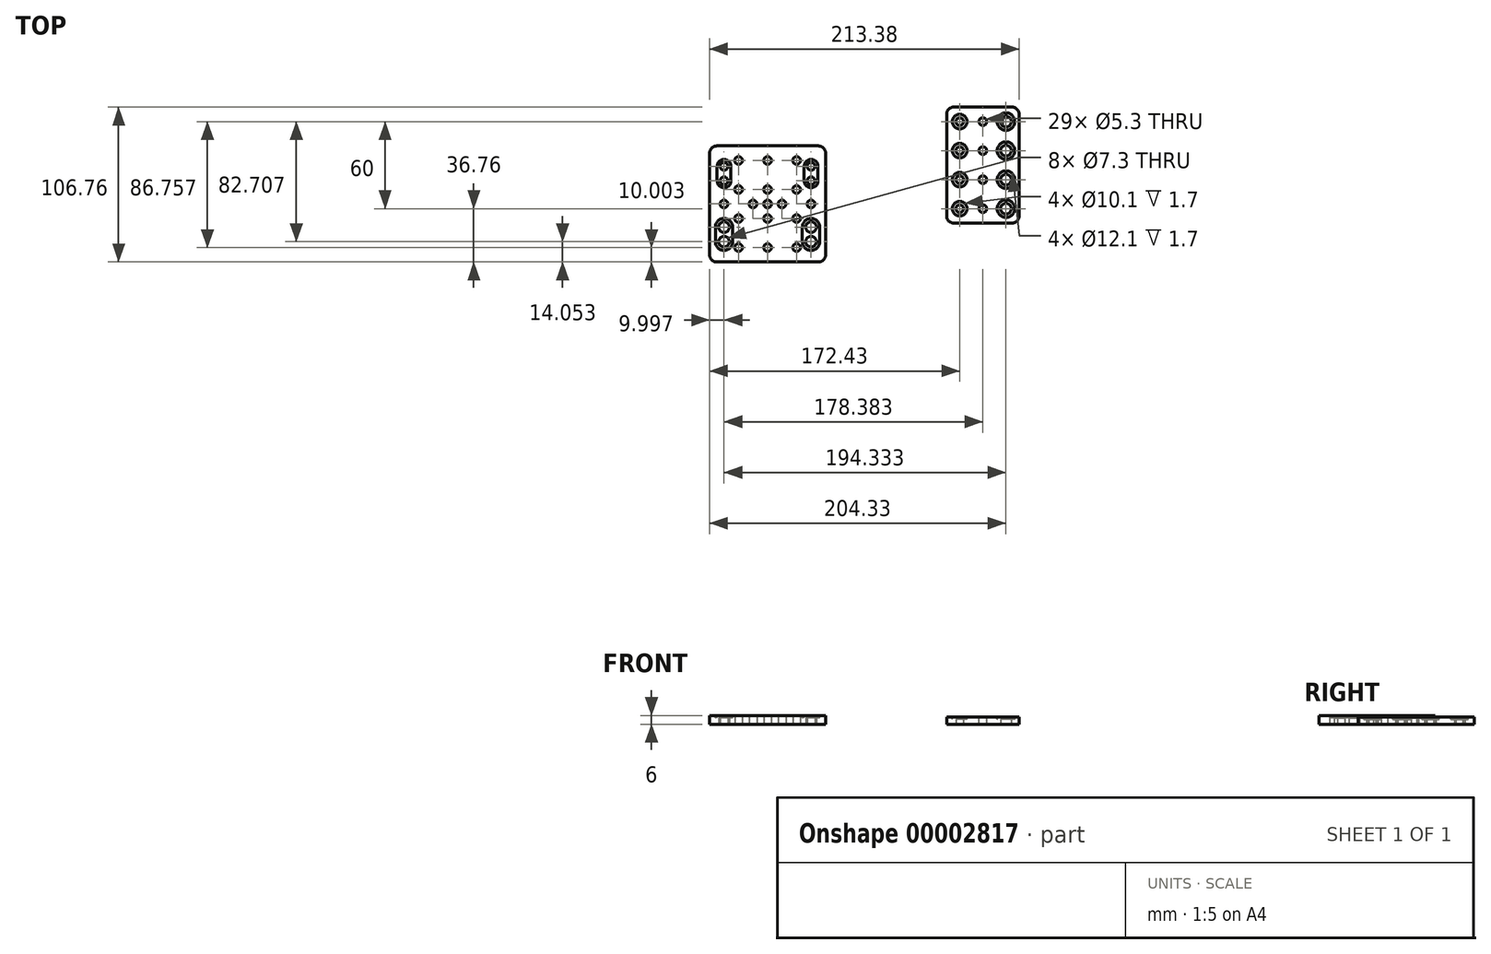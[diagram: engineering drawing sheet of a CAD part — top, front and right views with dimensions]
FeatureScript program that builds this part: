
annotation { "Feature Type Name" : "Feature", "Feature Type Description" : "" }
export const myFeature = defineFeature(function(context is Context, id is Id, definition is map)
    precondition{}
    {
        {
            var Q0;
            Q0=qCreatedBy(makeId("Top.planeOp"),FACE);
            var sketch = newSketch(context, id + "F0", { "sketchPlane" : qUnion([Q0])});
            skLineSegment(sketch, "E0.rect.bottom", {"start": v(-15.95, 60) * mm, "end": v(15.95, 60) * mm, "construction": true});
            skLineSegment(sketch, "E0.rect.top", {"start": v(-15.95, -60) * mm, "end": v(15.95, -60) * mm, "construction": true});
            skLineSegment(sketch, "E0.rect.left", {"start": v(-15.95, 60) * mm, "end": v(-15.95, -60) * mm, "construction": true});
            skLineSegment(sketch, "E0.rect.right", {"start": v(15.95, 60) * mm, "end": v(15.95, -60) * mm, "construction": true});
            skPoint(sketch, "E0.rect.middle", {"position": v(0, 0) * mm});
            skLineSegment(sketch, "E1.rect.bottom", {"start": v(-20, 40) * mm, "end": v(20, 40) * mm});
            skLineSegment(sketch, "E1.rect.top", {"start": v(-20, -40) * mm, "end": v(20, -40) * mm});
            skLineSegment(sketch, "E1.rect.left", {"start": v(-25, 35) * mm, "end": v(-25, -35) * mm});
            skLineSegment(sketch, "E1.rect.right", {"start": v(25, 35) * mm, "end": v(25, -35) * mm});
            skPoint(sketch, "E2.visualSharp", {"position": v(-25, 40) * mm});
            skArc(sketch, "E2.filletArc", {"start": v(-20, 40) * mm, "mid": v(-23.54, 38.54) * mm, "end": v(-25, 35) * mm});
            skPoint(sketch, "E3.visualSharp", {"position": v(25, 40) * mm});
            skArc(sketch, "E3.filletArc", {"start": v(25, 35) * mm, "mid": v(23.54, 38.54) * mm, "end": v(20, 40) * mm});
            skPoint(sketch, "E4.visualSharp", {"position": v(25, -40) * mm});
            skArc(sketch, "E4.filletArc", {"start": v(20, -40) * mm, "mid": v(23.54, -38.54) * mm, "end": v(25, -35) * mm});
            skPoint(sketch, "E5.visualSharp", {"position": v(-25, -40) * mm});
            skArc(sketch, "E5.filletArc", {"start": v(-25, -35) * mm, "mid": v(-23.54, -38.54) * mm, "end": v(-20, -40) * mm});
            skLineSegment(sketch, "E6", {"start": v(0, 40) * mm, "end": v(0, -40) * mm, "construction": true});
            skLineSegment(sketch, "E7", {"start": v(25, 0) * mm, "end": v(-25, 0) * mm, "construction": true});
            skPoint(sketch, "E8", {"position": v(-15.95, 10) * mm});
            skPoint(sketch, "E9", {"position": v(-15.95, 30) * mm});
            skPoint(sketch, "E10", {"position": v(-15.95, -10) * mm});
            skPoint(sketch, "E11", {"position": v(-15.95, -30) * mm});
            skPoint(sketch, "E12.MirrorP", {"position": v(15.95, 30) * mm});
            skPoint(sketch, "E13.MirrorP", {"position": v(15.95, 10) * mm});
            skPoint(sketch, "E14.MirrorP", {"position": v(15.95, -10) * mm});
            skPoint(sketch, "E15.MirrorP", {"position": v(15.95, -30) * mm});
            skCircle(sketch, "E16", {"center": v(-15.95, 30) * mm, "radius": 2.65 * mm});
            skCircle(sketch, "E17", {"center": v(-15.95, 10) * mm, "radius": 2.65 * mm});
            skCircle(sketch, "E18", {"center": v(-15.95, -10) * mm, "radius": 2.65 * mm});
            skCircle(sketch, "E19", {"center": v(-15.95, -30) * mm, "radius": 2.65 * mm});
            skCircle(sketch, "E20", {"center": v(15.95, 30) * mm, "radius": 3.65 * mm});
            skCircle(sketch, "E21", {"center": v(15.95, 10) * mm, "radius": 3.65 * mm});
            skCircle(sketch, "E22", {"center": v(15.95, -10) * mm, "radius": 3.65 * mm});
            skCircle(sketch, "E23", {"center": v(15.95, -30) * mm, "radius": 3.65 * mm});
            skSolve(sketch);
        }
        {
            var Q0;
            Q0 = qSketchRegion(id + "F0", true);
            extrude(context, id + "F1", {"entities" : qUnion([Q0]), "depth" : 5 * mm});
        }
        {
            var Q0;
            Q0=makeQuery(id+"F1.opExtrude","CAP_FACE",FACE,{"disambiguationData":[OSD([sQuery(id+"F0.wireOp",EDGE,"E1.rect.bottom"),sQuery(id+"F0.wireOp",EDGE,"E1.rect.top"),sQuery(id+"F0.wireOp",EDGE,"E1.rect.left"),sQuery(id+"F0.wireOp",EDGE,"E1.rect.right"),sQuery(id+"F0.wireOp",EDGE,"E2.filletArc"),sQuery(id+"F0.wireOp",EDGE,"E3.filletArc"),sQuery(id+"F0.wireOp",EDGE,"E4.filletArc"),sQuery(id+"F0.wireOp",EDGE,"E5.filletArc"),sQuery(id+"F0.wireOp",EDGE,"E16"),sQuery(id+"F0.wireOp",EDGE,"E17"),sQuery(id+"F0.wireOp",EDGE,"E18"),sQuery(id+"F0.wireOp",EDGE,"E19"),sQuery(id+"F0.wireOp",EDGE,"E20"),sQuery(id+"F0.wireOp",EDGE,"E21"),sQuery(id+"F0.wireOp",EDGE,"E22"),sQuery(id+"F0.wireOp",EDGE,"E23")])],"isStart":false});
            var sketch = newSketch(context, id + "F2", { "sketchPlane" : qUnion([Q0])});
            skCircle(sketch, "E24", {"center": v(-15.95, 30) * mm, "radius": 5.05 * mm});
            skCircle(sketch, "E25", {"center": v(-15.95, 10) * mm, "radius": 5.05 * mm});
            skCircle(sketch, "E26", {"center": v(-15.95, -10) * mm, "radius": 5.05 * mm});
            skCircle(sketch, "E27", {"center": v(-15.95, -30) * mm, "radius": 5.05 * mm});
            skCircle(sketch, "E28", {"center": v(15.95, 30) * mm, "radius": 6.05 * mm});
            skCircle(sketch, "E29", {"center": v(15.95, 10) * mm, "radius": 6.05 * mm});
            skCircle(sketch, "E30", {"center": v(15.95, -10) * mm, "radius": 6.05 * mm});
            skCircle(sketch, "E31", {"center": v(15.95, -30) * mm, "radius": 6.05 * mm});
            skSolve(sketch);
        }
        {
            var Q0;
            Q0 = qSketchRegion(id + "F2", true);
            extrude(context, id + "F3", {"entities" : qUnion([Q0]), "operationType" : NewBodyOperationType.REMOVE, "oppositeDirection" : true, "depth" : 1.7 * mm});
        }
        {
            var Q0;
            Q0=makeQuery(id+"F1.opExtrude","CAP_FACE",FACE,{"disambiguationData":[OSD([sQuery(id+"F0.wireOp",EDGE,"E1.rect.bottom"),sQuery(id+"F0.wireOp",EDGE,"E1.rect.top"),sQuery(id+"F0.wireOp",EDGE,"E1.rect.left"),sQuery(id+"F0.wireOp",EDGE,"E1.rect.right"),sQuery(id+"F0.wireOp",EDGE,"E2.filletArc"),sQuery(id+"F0.wireOp",EDGE,"E3.filletArc"),sQuery(id+"F0.wireOp",EDGE,"E4.filletArc"),sQuery(id+"F0.wireOp",EDGE,"E5.filletArc"),sQuery(id+"F0.wireOp",EDGE,"E16"),sQuery(id+"F0.wireOp",EDGE,"E17"),sQuery(id+"F0.wireOp",EDGE,"E18"),sQuery(id+"F0.wireOp",EDGE,"E19"),sQuery(id+"F0.wireOp",EDGE,"E20"),sQuery(id+"F0.wireOp",EDGE,"E21"),sQuery(id+"F0.wireOp",EDGE,"E22"),sQuery(id+"F0.wireOp",EDGE,"E23")])],"isStart":false});
            var sketch = newSketch(context, id + "F4", { "sketchPlane" : qUnion([Q0])});
            skLineSegment(sketch, "E32", {"start": v(0, 40) * mm, "end": v(0, -40) * mm, "construction": true});
            skPoint(sketch, "E33", {"position": v(0, 30) * mm});
            skPoint(sketch, "E34", {"position": v(0, 10) * mm});
            skPoint(sketch, "E35", {"position": v(0, -10) * mm});
            skPoint(sketch, "E36", {"position": v(0, -30) * mm});
            skCircle(sketch, "E37.0", {"center": v(-15.95, 30) * mm, "radius": 2.65 * mm, "construction": true});
            skCircle(sketch, "E38.0", {"center": v(-15.95, 10) * mm, "radius": 2.65 * mm, "construction": true});
            skCircle(sketch, "E39.0", {"center": v(-15.95, -10) * mm, "radius": 2.65 * mm, "construction": true});
            skCircle(sketch, "E40.0", {"center": v(-15.95, -30) * mm, "radius": 2.65 * mm, "construction": true});
            skCircle(sketch, "E41", {"center": v(0, 30) * mm, "radius": 2.65 * mm});
            skCircle(sketch, "E42", {"center": v(0, 10) * mm, "radius": 2.65 * mm});
            skCircle(sketch, "E43", {"center": v(0, -10) * mm, "radius": 2.65 * mm});
            skCircle(sketch, "E44", {"center": v(0, -30) * mm, "radius": 2.65 * mm});
            skSolve(sketch);
        }
        {
            var Q0;
            Q0 = qSketchRegion(id + "F4", true);
            var Q1;
            Q1=makeQuery(id+"F1.opExtrude","CAP_FACE",FACE,{"disambiguationData":[OSD([sQuery(id+"F0.wireOp",EDGE,"E1.rect.bottom"),sQuery(id+"F0.wireOp",EDGE,"E1.rect.top"),sQuery(id+"F0.wireOp",EDGE,"E1.rect.left"),sQuery(id+"F0.wireOp",EDGE,"E1.rect.right"),sQuery(id+"F0.wireOp",EDGE,"E2.filletArc"),sQuery(id+"F0.wireOp",EDGE,"E3.filletArc"),sQuery(id+"F0.wireOp",EDGE,"E4.filletArc"),sQuery(id+"F0.wireOp",EDGE,"E5.filletArc"),sQuery(id+"F0.wireOp",EDGE,"E16"),sQuery(id+"F0.wireOp",EDGE,"E17"),sQuery(id+"F0.wireOp",EDGE,"E18"),sQuery(id+"F0.wireOp",EDGE,"E19"),sQuery(id+"F0.wireOp",EDGE,"E20"),sQuery(id+"F0.wireOp",EDGE,"E21"),sQuery(id+"F0.wireOp",EDGE,"E22"),sQuery(id+"F0.wireOp",EDGE,"E23")])],"isStart":true});
            extrude(context, id + "F5", {"entities" : qUnion([Q0]), "operationType" : NewBodyOperationType.REMOVE, "endBound" : BoundingType.UP_TO_SURFACE, "oppositeDirection" : true, "endBoundEntityFace" : qUnion([Q1]), "depth" : 25 * mm});
        }
        {
            var Q0;
            Q0=qCreatedBy(makeId("Top.planeOp"),FACE);
            var sketch = newSketch(context, id + "F6", { "sketchPlane" : qUnion([Q0])});
            skLineSegment(sketch, "E45", {"start": v(-148.38, 31.47) * mm, "end": v(-148.38, -84.99) * mm, "construction": true});
            skLineSegment(sketch, "E46", {"start": v(-200.91, -26.76) * mm, "end": v(-92.3, -26.76) * mm, "construction": true});
            skPoint(sketch, "E46.startSnap0", {"position": v(-148.38, -26.76) * mm});
            skPoint(sketch, "E47", {"position": v(-178.38, -10.8) * mm});
            skPoint(sketch, "E48", {"position": v(-178.38, -42.7) * mm});
            skPoint(sketch, "E49", {"position": v(-178.38, -52.7) * mm});
            skPoint(sketch, "E50", {"position": v(-178.38, -0.8) * mm});
            skPoint(sketch, "E51", {"position": v(-118.38, -10.8) * mm});
            skPoint(sketch, "E52", {"position": v(-118.38, -0.8) * mm});
            skPoint(sketch, "E53", {"position": v(-118.38, -42.7) * mm});
            skPoint(sketch, "E54", {"position": v(-118.38, -52.7) * mm});
            skCircle(sketch, "E55", {"center": v(-178.38, -0.8) * mm, "radius": 2.65 * mm});
            skCircle(sketch, "E56", {"center": v(-178.38, -10.8) * mm, "radius": 2.65 * mm});
            skCircle(sketch, "E57", {"center": v(-178.38, -42.7) * mm, "radius": 3.65 * mm});
            skCircle(sketch, "E58", {"center": v(-178.38, -52.7) * mm, "radius": 3.65 * mm});
            skCircle(sketch, "E59", {"center": v(-118.38, -0.8) * mm, "radius": 2.65 * mm});
            skCircle(sketch, "E60", {"center": v(-118.38, -10.8) * mm, "radius": 2.65 * mm});
            skCircle(sketch, "E61", {"center": v(-118.38, -42.7) * mm, "radius": 3.65 * mm});
            skCircle(sketch, "E62", {"center": v(-118.38, -52.7) * mm, "radius": 3.65 * mm});
            skPoint(sketch, "E63", {"position": v(-158.38, -26.76) * mm});
            skPoint(sketch, "E64", {"position": v(-178.38, -26.76) * mm});
            skPoint(sketch, "E65", {"position": v(-138.38, -26.76) * mm});
            skPoint(sketch, "E66", {"position": v(-118.38, -26.76) * mm});
            skCircle(sketch, "E67", {"center": v(-178.38, -26.76) * mm, "radius": 2.65 * mm});
            skCircle(sketch, "E68", {"center": v(-158.38, -26.76) * mm, "radius": 2.65 * mm});
            skCircle(sketch, "E69", {"center": v(-148.38, -26.76) * mm, "radius": 2.65 * mm});
            skCircle(sketch, "E70", {"center": v(-138.38, -26.76) * mm, "radius": 2.65 * mm});
            skCircle(sketch, "E71", {"center": v(-118.38, -26.76) * mm, "radius": 2.65 * mm});
            skPoint(sketch, "E72", {"position": v(-148.38, -16.76) * mm});
            skPoint(sketch, "E73", {"position": v(-148.38, -36.76) * mm});
            skPoint(sketch, "E74", {"position": v(-168.38, -36.76) * mm});
            skPoint(sketch, "E75", {"position": v(-168.38, -16.76) * mm});
            skPoint(sketch, "E76", {"position": v(-128.38, -16.76) * mm});
            skPoint(sketch, "E77", {"position": v(-128.38, -36.76) * mm});
            skCircle(sketch, "E78", {"center": v(-168.38, -16.76) * mm, "radius": 2.65 * mm});
            skCircle(sketch, "E79", {"center": v(-148.38, -16.76) * mm, "radius": 2.65 * mm});
            skCircle(sketch, "E80", {"center": v(-128.38, -16.76) * mm, "radius": 2.65 * mm});
            skCircle(sketch, "E81", {"center": v(-128.38, -36.76) * mm, "radius": 2.65 * mm});
            skCircle(sketch, "E82", {"center": v(-148.38, -36.76) * mm, "radius": 2.65 * mm});
            skCircle(sketch, "E83", {"center": v(-168.38, -36.76) * mm, "radius": 2.65 * mm});
            skCircle(sketch, "E84.0.1.0", {"center": v(-168.38, 3.24) * mm, "radius": 2.65 * mm});
            skCircle(sketch, "E84.0.1.1", {"center": v(-148.38, 3.24) * mm, "radius": 2.65 * mm});
            skCircle(sketch, "E84.0.1.2", {"center": v(-128.38, 3.24) * mm, "radius": 2.65 * mm});
            skLineSegment(sketch, "E84.direction1", {"start": v(-168.38, -16.76) * mm, "end": v(-143.38, -16.76) * mm, "construction": true});
            skLineSegment(sketch, "E84.direction2", {"start": v(-168.38, -16.76) * mm, "end": v(-168.38, 3.24) * mm, "construction": true});
            skCircle(sketch, "E85.0.1.0", {"center": v(-168.38, -56.76) * mm, "radius": 2.65 * mm});
            skCircle(sketch, "E85.0.1.1", {"center": v(-148.38, -56.76) * mm, "radius": 2.65 * mm});
            skCircle(sketch, "E85.0.1.2", {"center": v(-128.38, -56.76) * mm, "radius": 2.65 * mm});
            skLineSegment(sketch, "E85.direction1", {"start": v(-168.38, -36.76) * mm, "end": v(-143.38, -36.76) * mm, "construction": true});
            skLineSegment(sketch, "E85.direction2", {"start": v(-168.38, -36.76) * mm, "end": v(-168.38, -56.76) * mm, "construction": true});
            skLineSegment(sketch, "E86.rect.bottom", {"start": v(-188.38, 13.24) * mm, "end": v(-108.38, 13.24) * mm});
            skLineSegment(sketch, "E86.rect.top", {"start": v(-188.38, -66.76) * mm, "end": v(-108.38, -66.76) * mm});
            skLineSegment(sketch, "E86.rect.left", {"start": v(-188.38, 13.24) * mm, "end": v(-188.38, -66.76) * mm});
            skLineSegment(sketch, "E86.rect.right", {"start": v(-108.38, 13.24) * mm, "end": v(-108.38, -66.76) * mm});
            skSolve(sketch);
        }
        {
            var Q0;
            Q0 = qSketchRegion(id + "F6", true);
            extrude(context, id + "F7", {"entities" : qUnion([Q0]), "depth" : 6 * mm});
        }
        {
            var Q0;
            Q0=makeQuery(id+"F7.opExtrude","CAP_FACE",FACE,{"disambiguationData":[OSD([sQuery(id+"F6.wireOp",EDGE,"E55"),sQuery(id+"F6.wireOp",EDGE,"E56"),sQuery(id+"F6.wireOp",EDGE,"E57"),sQuery(id+"F6.wireOp",EDGE,"E58"),sQuery(id+"F6.wireOp",EDGE,"E59"),sQuery(id+"F6.wireOp",EDGE,"E60"),sQuery(id+"F6.wireOp",EDGE,"E61"),sQuery(id+"F6.wireOp",EDGE,"E62"),sQuery(id+"F6.wireOp",EDGE,"E67"),sQuery(id+"F6.wireOp",EDGE,"E68"),sQuery(id+"F6.wireOp",EDGE,"E69"),sQuery(id+"F6.wireOp",EDGE,"E70"),sQuery(id+"F6.wireOp",EDGE,"E71"),sQuery(id+"F6.wireOp",EDGE,"E78"),sQuery(id+"F6.wireOp",EDGE,"E79"),sQuery(id+"F6.wireOp",EDGE,"E80"),sQuery(id+"F6.wireOp",EDGE,"E81"),sQuery(id+"F6.wireOp",EDGE,"E82"),sQuery(id+"F6.wireOp",EDGE,"E83"),sQuery(id+"F6.wireOp",EDGE,"E84.0.1.0"),sQuery(id+"F6.wireOp",EDGE,"E84.0.1.1"),sQuery(id+"F6.wireOp",EDGE,"E84.0.1.2"),sQuery(id+"F6.wireOp",EDGE,"E85.0.1.0"),sQuery(id+"F6.wireOp",EDGE,"E85.0.1.1"),sQuery(id+"F6.wireOp",EDGE,"E85.0.1.2"),sQuery(id+"F6.wireOp",EDGE,"E86.rect.bottom"),sQuery(id+"F6.wireOp",EDGE,"E86.rect.top"),sQuery(id+"F6.wireOp",EDGE,"E86.rect.left"),sQuery(id+"F6.wireOp",EDGE,"E86.rect.right")])],"isStart":false});
            var sketch = newSketch(context, id + "F8", { "sketchPlane" : qUnion([Q0])});
            skLineSegment(sketch, "E87", {"start": v(-188.38, -26.76) * mm, "end": v(-108.38, -26.76) * mm, "construction": true});
            skLineSegment(sketch, "E88", {"start": v(-148.38, 13.24) * mm, "end": v(-148.38, -66.76) * mm, "construction": true});
            skCircle(sketch, "E89.0", {"center": v(-178.38, -42.7) * mm, "radius": 3.65 * mm, "construction": true});
            skCircle(sketch, "E90.0", {"center": v(-178.38, -52.7) * mm, "radius": 3.65 * mm, "construction": true});
            skCircle(sketch, "E91.0", {"center": v(-118.38, -52.7) * mm, "radius": 3.65 * mm, "construction": true});
            skCircle(sketch, "E92.0", {"center": v(-118.38, -42.7) * mm, "radius": 3.65 * mm, "construction": true});
            skCircle(sketch, "E93.0", {"center": v(-178.38, -10.8) * mm, "radius": 2.65 * mm, "construction": true});
            skCircle(sketch, "E94.0", {"center": v(-178.38, -0.8) * mm, "radius": 2.65 * mm, "construction": true});
            skCircle(sketch, "E95.0", {"center": v(-118.38, -0.8) * mm, "radius": 2.65 * mm, "construction": true});
            skCircle(sketch, "E96.0", {"center": v(-118.38, -10.8) * mm, "radius": 2.65 * mm, "construction": true});
            skArc(sketch, "E97", {"start": v(-173.63, -0.8) * mm, "mid": v(-178.38, 3.94) * mm, "end": v(-183.13, -0.8) * mm});
            skArc(sketch, "E98", {"start": v(-183.13, -10.8) * mm, "mid": v(-178.38, -15.56) * mm, "end": v(-173.63, -10.8) * mm});
            skArc(sketch, "E99", {"start": v(-172.38, -42.7) * mm, "mid": v(-178.38, -36.7) * mm, "end": v(-184.38, -42.7) * mm});
            skArc(sketch, "E100", {"start": v(-184.38, -52.7) * mm, "mid": v(-178.38, -58.7) * mm, "end": v(-172.38, -52.7) * mm});
            skArc(sketch, "E101", {"start": v(-112.38, -42.7) * mm, "mid": v(-118.38, -36.7) * mm, "end": v(-124.38, -42.7) * mm});
            skArc(sketch, "E102", {"start": v(-124.38, -52.7) * mm, "mid": v(-118.38, -58.7) * mm, "end": v(-112.38, -52.7) * mm});
            skArc(sketch, "E103", {"start": v(-123.13, -10.8) * mm, "mid": v(-118.38, -15.56) * mm, "end": v(-113.63, -10.8) * mm});
            skArc(sketch, "E104", {"start": v(-113.63, -0.8) * mm, "mid": v(-118.38, 3.94) * mm, "end": v(-123.13, -0.8) * mm});
            skLineSegment(sketch, "E105", {"start": v(-183.13, -0.8) * mm, "end": v(-183.13, -10.8) * mm});
            skLineSegment(sketch, "E106", {"start": v(-173.63, -10.8) * mm, "end": v(-173.63, -0.8) * mm});
            skLineSegment(sketch, "E107", {"start": v(-123.13, -0.8) * mm, "end": v(-123.13, -10.8) * mm});
            skLineSegment(sketch, "E108", {"start": v(-113.63, -10.8) * mm, "end": v(-113.63, -0.8) * mm});
            skLineSegment(sketch, "E109", {"start": v(-184.38, -42.7) * mm, "end": v(-184.38, -52.7) * mm});
            skLineSegment(sketch, "E110", {"start": v(-172.38, -52.7) * mm, "end": v(-172.38, -42.7) * mm});
            skLineSegment(sketch, "E111", {"start": v(-124.38, -42.7) * mm, "end": v(-124.38, -52.7) * mm});
            skLineSegment(sketch, "E112", {"start": v(-112.38, -52.7) * mm, "end": v(-112.38, -42.7) * mm});
            skSolve(sketch);
        }
        {
            var Q0;
            Q0 = qSketchRegion(id + "F8", true);
            extrude(context, id + "F9", {"entities" : qUnion([Q0]), "operationType" : NewBodyOperationType.REMOVE, "oppositeDirection" : true, "depth" : 1.6 * mm});
        }
        {
            var Q0;
            Q0=makeQuery(id+"F7.opExtrude","SWEPT_EDGE",EDGE,{"disambiguationData":[OSD([sQuery(id+"F6.wireOp",EDGE,"E86.rect.bottom"),sQuery(id+"F6.wireOp",EDGE,"E86.rect.left")])]});
            var Q1;
            Q1=makeQuery(id+"F7.opExtrude","SWEPT_EDGE",EDGE,{"disambiguationData":[OSD([sQuery(id+"F6.wireOp",EDGE,"E86.rect.bottom"),sQuery(id+"F6.wireOp",EDGE,"E86.rect.right")])]});
            var Q2;
            Q2=makeQuery(id+"F7.opExtrude","SWEPT_EDGE",EDGE,{"disambiguationData":[OSD([sQuery(id+"F6.wireOp",EDGE,"E86.rect.top"),sQuery(id+"F6.wireOp",EDGE,"E86.rect.right")])]});
            var Q3;
            Q3=makeQuery(id+"F7.opExtrude","SWEPT_EDGE",EDGE,{"disambiguationData":[OSD([sQuery(id+"F6.wireOp",EDGE,"E86.rect.top"),sQuery(id+"F6.wireOp",EDGE,"E86.rect.left")])]});
            fillet(context, id + "F10", {"entities" : qUnion([Q0, Q1, Q2, Q3]), "radius" : 5 * mm, "tangentPropagation" : true, "allowEdgeOverflow" : false});
        }
    });
